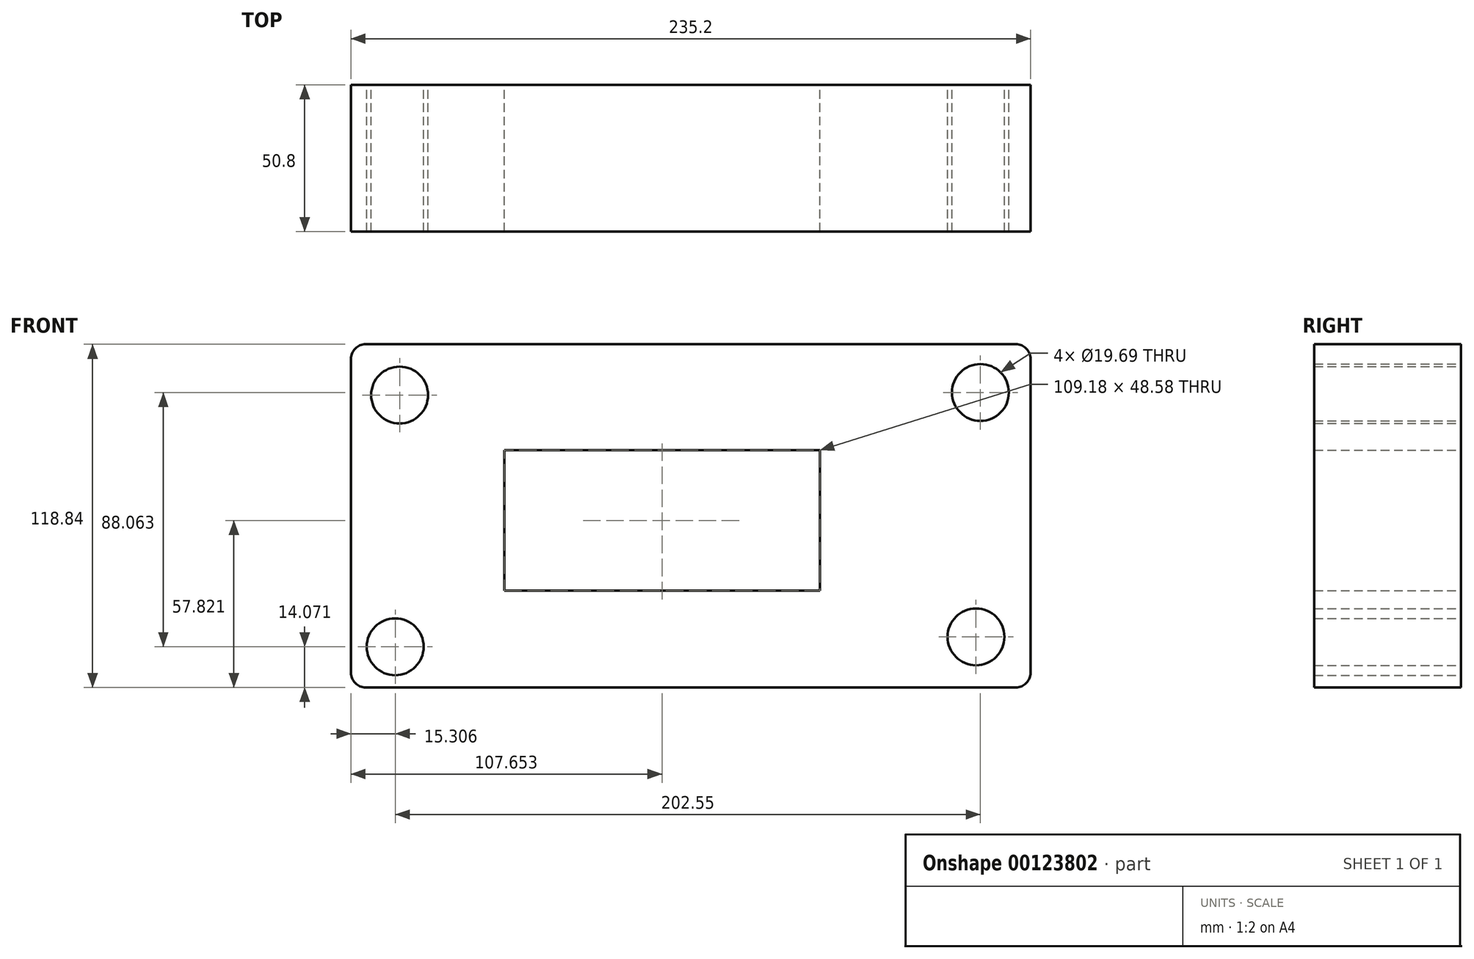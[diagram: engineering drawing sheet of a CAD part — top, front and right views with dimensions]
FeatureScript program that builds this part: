
annotation { "Feature Type Name" : "Feature", "Feature Type Description" : "" }
export const myFeature = defineFeature(function(context is Context, id is Id, definition is map)
    precondition{}
    {
        {
            var Q0;
            Q0=qCreatedBy(makeId("Front.planeOp"),FACE);
            var sketch = newSketch(context, id + "F0", { "sketchPlane" : qUnion([Q0])});
            skLineSegment(sketch, "E0.bottom", {"start": v(-125, 51.93) * mm, "end": v(110.2, 51.93) * mm});
            skLineSegment(sketch, "E0.top", {"start": v(-125, -66.91) * mm, "end": v(110.2, -66.91) * mm});
            skLineSegment(sketch, "E0.left", {"start": v(-125, 51.93) * mm, "end": v(-125, -66.91) * mm});
            skLineSegment(sketch, "E0.right", {"start": v(110.2, 51.93) * mm, "end": v(110.2, -66.91) * mm});
            skCircle(sketch, "E1", {"center": v(91.33, -49.4) * mm, "radius": 9.84 * mm});
            skCircle(sketch, "E2", {"center": v(92.86, 35.22) * mm, "radius": 9.84 * mm});
            skCircle(sketch, "E3", {"center": v(-109.7, -52.84) * mm, "radius": 9.84 * mm});
            skCircle(sketch, "E4", {"center": v(-108.16, 34.34) * mm, "radius": 9.84 * mm});
            skLineSegment(sketch, "E5.bottom", {"start": v(-71.94, 15.2) * mm, "end": v(37.24, 15.2) * mm});
            skLineSegment(sketch, "E5.top", {"start": v(-71.94, -33.38) * mm, "end": v(37.24, -33.38) * mm});
            skLineSegment(sketch, "E5.left", {"start": v(-71.94, 15.2) * mm, "end": v(-71.94, -33.38) * mm});
            skLineSegment(sketch, "E5.right", {"start": v(37.24, 15.2) * mm, "end": v(37.24, -33.38) * mm});
            skSolve(sketch);
        }
        {
            var Q0;
            Q0=makeQuery(id+"F0.imprint","IMPRINT",FACE,{"disambiguationData":[TD([[makeQuery(id+"F0.imprint","IMPRINT",EDGE,{"derivedFrom":sQuery(id+"F0.wireOp",EDGE,"E0.bottom")}),-1.0]])]});
            extrude(context, id + "F1", {"entities" : qUnion([Q0]), "depth" : 50.8 * mm});
        }
        {
            var Q0;
            Q0=makeQuery(id+"F1.opExtrude","SWEPT_EDGE",EDGE,{"disambiguationData":[OSD([sQuery(id+"F0.wireOp",EDGE,"E0.top"),sQuery(id+"F0.wireOp",EDGE,"E0.right")])]});
            var Q1;
            Q1=makeQuery(id+"F1.opExtrude","SWEPT_EDGE",EDGE,{"disambiguationData":[OSD([sQuery(id+"F0.wireOp",EDGE,"E0.top"),sQuery(id+"F0.wireOp",EDGE,"E0.left")])]});
            fillet(context, id + "F2", {"entities" : qUnion([Q0, Q1]), "radius" : 5.08 * mm, "tangentPropagation" : true, "allowEdgeOverflow" : false});
        }
        {
            var Q0;
            Q0=makeQuery(id+"F1.opExtrude","SWEPT_EDGE",EDGE,{"disambiguationData":[OSD([sQuery(id+"F0.wireOp",EDGE,"E0.bottom"),sQuery(id+"F0.wireOp",EDGE,"E0.left")])]});
            fillet(context, id + "F3", {"entities" : qUnion([Q0]), "radius" : 5.08 * mm, "tangentPropagation" : true, "allowEdgeOverflow" : false});
        }
        {
            var Q0;
            Q0=makeQuery(id+"F1.opExtrude","SWEPT_EDGE",EDGE,{"disambiguationData":[OSD([sQuery(id+"F0.wireOp",EDGE,"E0.bottom"),sQuery(id+"F0.wireOp",EDGE,"E0.right")])]});
            fillet(context, id + "F4", {"entities" : qUnion([Q0]), "radius" : 5.08 * mm, "tangentPropagation" : true, "allowEdgeOverflow" : false});
        }
    });
